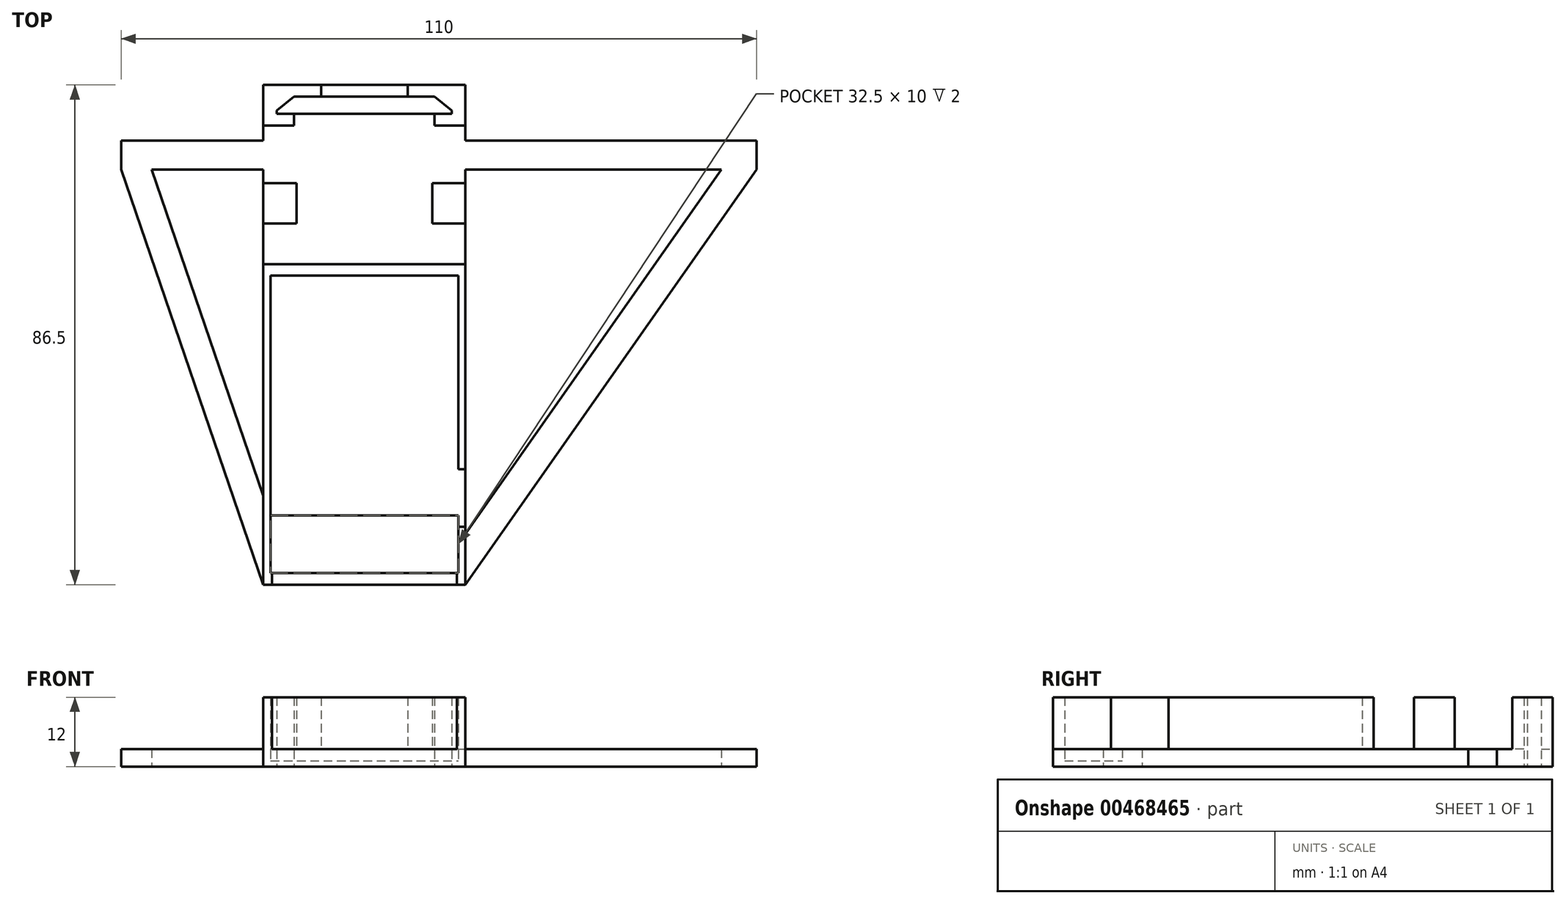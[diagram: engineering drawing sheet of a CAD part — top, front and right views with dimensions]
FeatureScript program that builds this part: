
annotation { "Feature Type Name" : "Feature", "Feature Type Description" : "" }
export const myFeature = defineFeature(function(context is Context, id is Id, definition is map)
    precondition{}
    {
        {
            var Q0;
            Q0=qCreatedBy(makeId("Top.planeOp"),FACE);
            var sketch = newSketch(context, id + "F0", { "sketchPlane" : qUnion([Q0])});
            skLineSegment(sketch, "E0", {"start": v(0, 43.25) * mm, "end": v(-17.5, 43.25) * mm});
            skLineSegment(sketch, "E1", {"start": v(-17.5, 43.25) * mm, "end": v(-17.5, 0) * mm});
            skLineSegment(sketch, "E2", {"start": v(-17.5, 0) * mm, "end": v(-17.5, -43.25) * mm});
            skLineSegment(sketch, "E3", {"start": v(-17.5, 33.6) * mm, "end": v(-42.1, 33.6) * mm});
            skLineSegment(sketch, "E4", {"start": v(-42.1, 33.6) * mm, "end": v(-42.1, 28.6) * mm});
            skLineSegment(sketch, "E5", {"start": v(-42.1, 28.6) * mm, "end": v(-17.5, 28.6) * mm});
            skLineSegment(sketch, "E6", {"start": v(-17.5, -43.25) * mm, "end": v(0, -43.25) * mm});
            skLineSegment(sketch, "E7", {"start": v(-42.1, 28.6) * mm, "end": v(-17.5, -43.25) * mm});
            skLineSegment(sketch, "E8", {"start": v(-17.5, -43.25) * mm, "end": v(-17.5, -27.82) * mm});
            skLineSegment(sketch, "E9", {"start": v(-17.5, -27.82) * mm, "end": v(-36.82, 28.6) * mm});
            skLineSegment(sketch, "E10", {"start": v(-37.1, 33.6) * mm, "end": v(-37.1, 28.6) * mm});
            skLineSegment(sketch, "E11.MirrorCS", {"start": v(17.5, -34.54) * mm, "end": v(61.78, 28.6) * mm});
            skLineSegment(sketch, "E12.MirrorCS", {"start": v(17.5, -43.25) * mm, "end": v(17.5, -34.54) * mm});
            skLineSegment(sketch, "E13.MirrorCS", {"start": v(0, 43.25) * mm, "end": v(17.5, 43.25) * mm});
            skLineSegment(sketch, "E14.MirrorCS", {"start": v(67.9, 28.6) * mm, "end": v(17.5, -43.25) * mm});
            skLineSegment(sketch, "E15.MirrorCS", {"start": v(17.5, 43.25) * mm, "end": v(17.5, 0) * mm});
            skLineSegment(sketch, "E16.MirrorCS", {"start": v(17.5, 0) * mm, "end": v(17.5, -43.25) * mm});
            skLineSegment(sketch, "E17.MirrorCS", {"start": v(62.9, 33.6) * mm, "end": v(62.9, 28.6) * mm});
            skLineSegment(sketch, "E18.MirrorCS", {"start": v(17.5, -43.25) * mm, "end": v(0, -43.25) * mm});
            skLineSegment(sketch, "E19.MirrorCS", {"start": v(67.9, 28.6) * mm, "end": v(17.5, 28.6) * mm});
            skLineSegment(sketch, "E20.MirrorCS", {"start": v(67.9, 33.6) * mm, "end": v(67.9, 28.6) * mm});
            skLineSegment(sketch, "E21.MirrorCS", {"start": v(17.5, 33.6) * mm, "end": v(67.9, 33.6) * mm});
            skLineSegment(sketch, "E22", {"start": v(0, 41.25) * mm, "end": v(12.15, 41.25) * mm});
            skLineSegment(sketch, "E23", {"start": v(12.15, 41.25) * mm, "end": v(15.15, 38.85) * mm});
            skLineSegment(sketch, "E24", {"start": v(15.15, 38.85) * mm, "end": v(15.15, 38.25) * mm});
            skLineSegment(sketch, "E25", {"start": v(15.15, 38.25) * mm, "end": v(0, 38.25) * mm});
            skLineSegment(sketch, "E26.MirrorCS", {"start": v(-15.15, 38.85) * mm, "end": v(-15.15, 38.25) * mm});
            skLineSegment(sketch, "E27.MirrorCS", {"start": v(0, 41.25) * mm, "end": v(-12.15, 41.25) * mm});
            skLineSegment(sketch, "E28.MirrorCS", {"start": v(-15.15, 38.25) * mm, "end": v(0, 38.25) * mm});
            skLineSegment(sketch, "E29.MirrorCS", {"start": v(-12.15, 41.25) * mm, "end": v(-15.15, 38.85) * mm});
            skLineSegment(sketch, "E30", {"start": v(-7.5, 43.25) * mm, "end": v(-7.5, 41.25) * mm});
            skLineSegment(sketch, "E31", {"start": v(-12.15, 36.25) * mm, "end": v(-17.5, 36.25) * mm});
            skLineSegment(sketch, "E32.MirrorCS", {"start": v(12.15, 36.25) * mm, "end": v(17.5, 36.25) * mm});
            skLineSegment(sketch, "E33.MirrorCS", {"start": v(7.5, 43.25) * mm, "end": v(7.5, 41.25) * mm});
            skLineSegment(sketch, "E34", {"start": v(0, -41.25) * mm, "end": v(-16.25, -41.25) * mm});
            skLineSegment(sketch, "E35", {"start": v(-16.25, -41.25) * mm, "end": v(-16.25, 10.25) * mm});
            skLineSegment(sketch, "E36", {"start": v(-16.25, 10.25) * mm, "end": v(0, 10.25) * mm});
            skLineSegment(sketch, "E37.MirrorCS", {"start": v(0, -41.25) * mm, "end": v(16.25, -41.25) * mm});
            skLineSegment(sketch, "E38.MirrorCS", {"start": v(16.25, 10.25) * mm, "end": v(0, 10.25) * mm});
            skLineSegment(sketch, "E39.MirrorCS", {"start": v(16.25, -41.25) * mm, "end": v(16.25, 10.25) * mm});
            skLineSegment(sketch, "E40", {"start": v(17.5, -33.25) * mm, "end": v(16.25, -33.25) * mm});
            skLineSegment(sketch, "E41", {"start": v(17.5, -23.25) * mm, "end": v(16.25, -23.25) * mm});
            skLineSegment(sketch, "E42", {"start": v(-16.25, -31.25) * mm, "end": v(16.25, -31.25) * mm});
            skLineSegment(sketch, "E43", {"start": v(-17.5, 12.25) * mm, "end": v(17.5, 12.25) * mm});
            skLineSegment(sketch, "E44", {"start": v(-16, -41.25) * mm, "end": v(-16, -43.25) * mm});
            skLineSegment(sketch, "E45.MirrorCS", {"start": v(16, -41.25) * mm, "end": v(16, -43.25) * mm});
            skLineSegment(sketch, "E46", {"start": v(-12.15, 36.25) * mm, "end": v(-12.15, 38.25) * mm});
            skLineSegment(sketch, "E47", {"start": v(12.15, 36.25) * mm, "end": v(12.15, 38.25) * mm});
            skLineSegment(sketch, "E48", {"start": v(-17.5, 26.25) * mm, "end": v(-11.75, 26.25) * mm});
            skLineSegment(sketch, "E49.MirrorCS", {"start": v(17.5, 26.25) * mm, "end": v(11.75, 26.25) * mm});
            skLineSegment(sketch, "E50", {"start": v(-11.75, 19.25) * mm, "end": v(-17.5, 19.25) * mm});
            skPoint(sketch, "E50.endSnap0", {"position": v(-17.5, 21.63) * mm});
            skLineSegment(sketch, "E51", {"start": v(11.75, 19.25) * mm, "end": v(17.5, 19.25) * mm});
            skLineSegment(sketch, "E52", {"start": v(-11.75, 26.25) * mm, "end": v(-11.75, 19.25) * mm});
            skLineSegment(sketch, "E53", {"start": v(11.75, 26.25) * mm, "end": v(11.75, 19.25) * mm});
            skSolve(sketch);
        }
        {
            var Q0;
            {var subQ7=sQuery(id+"F0.wireOp",EDGE,"E26.MirrorCS");Q0=makeQuery(id+"F0.imprint","IMPRINT",FACE,{"disambiguationData":[TD([[makeQuery(id+"F0.imprint","IMPRINT",EDGE,{"derivedFrom":subQ7}),-1.0]])]});}
            var Q1;
            {var subQ3=sQuery(id+"F0.wireOp",EDGE,"E30");Q1=makeQuery(id+"F0.imprint","IMPRINT",FACE,{"disambiguationData":[TD([[makeQuery(id+"F0.imprint","IMPRINT",EDGE,{"derivedFrom":subQ3}),1.0]])]});}
            var Q2;
            {var subQ0=sQuery(id+"F0.wireOp",EDGE,"E23");Q2=makeQuery(id+"F0.imprint","IMPRINT",FACE,{"disambiguationData":[TD([[makeQuery(id+"F0.imprint","IMPRINT",EDGE,{"derivedFrom":subQ0}),1.0]])]});}
            var Q3;
            {var subQ1=sQuery(id+"F0.wireOp",EDGE,"fqxOtDsU-wHGC-yRUm-2BCM-Caq6WvGUI0ms");Q3=makeQuery(id+"F0.imprint","IMPRINT",FACE,{"disambiguationData":[TD([[makeQuery(id+"F0.imprint","IMPRINT",EDGE,{"derivedFrom":subQ1}),1.0]])]});}
            var Q4;
            {var subQ9=sQuery(id+"F0.wireOp",EDGE,"E2");Q4=makeQuery(id+"F0.imprint","IMPRINT",FACE,{"disambiguationData":[TD([[makeQuery(id+"F0.imprint","IMPRINT",EDGE,{"derivedFrom":subQ9}),1.0]])]});}
            var Q5;
            {var subQ3=sQuery(id+"F0.wireOp",EDGE,"E40");Q5=makeQuery(id+"F0.imprint","IMPRINT",FACE,{"disambiguationData":[TD([[makeQuery(id+"F0.imprint","IMPRINT",EDGE,{"derivedFrom":subQ3}),-1.0]])]});}
            var Q6;
            {var subQ3=sQuery(id+"F0.wireOp",EDGE,"E11.MirrorCS");Q6=makeQuery(id+"F0.imprint","IMPRINT",FACE,{"disambiguationData":[TD([[makeQuery(id+"F0.imprint","IMPRINT",EDGE,{"derivedFrom":subQ3}),-1.0]])]});}
            var Q7;
            {var subQ2=sQuery(id+"F0.wireOp",EDGE,"E10");Q7=makeQuery(id+"F0.imprint","IMPRINT",FACE,{"disambiguationData":[TD([[makeQuery(id+"F0.imprint","IMPRINT",EDGE,{"derivedFrom":subQ2}),1.0]])]});}
            var Q8;
            {var subQ0=sQuery(id+"F0.wireOp",EDGE,"E4");Q8=makeQuery(id+"F0.imprint","IMPRINT",FACE,{"disambiguationData":[TD([[makeQuery(id+"F0.imprint","IMPRINT",EDGE,{"derivedFrom":subQ0}),1.0]])]});}
            var Q9;
            {var subQ0=sQuery(id+"F0.wireOp",EDGE,"E17.MirrorCS");Q9=makeQuery(id+"F0.imprint","IMPRINT",FACE,{"disambiguationData":[TD([[makeQuery(id+"F0.imprint","IMPRINT",EDGE,{"derivedFrom":subQ0}),1.0]])]});}
            var Q10;
            {var subQ6=sQuery(id+"F0.wireOp",EDGE,"E17.MirrorCS");Q10=makeQuery(id+"F0.imprint","IMPRINT",FACE,{"disambiguationData":[TD([[makeQuery(id+"F0.imprint","IMPRINT",EDGE,{"derivedFrom":subQ6}),-1.0]])]});}
            var Q11;
            {var subQ4=sQuery(id+"F0.wireOp",EDGE,"E36");Q11=makeQuery(id+"F0.imprint","IMPRINT",FACE,{"disambiguationData":[TD([[makeQuery(id+"F0.imprint","IMPRINT",EDGE,{"derivedFrom":subQ4}),-1.0]])]});}
            var Q12;
            {var subQ0=sQuery(id+"F0.wireOp",EDGE,"E7");Q12=makeQuery(id+"F0.imprint","IMPRINT",FACE,{"disambiguationData":[TD([[makeQuery(id+"F0.imprint","IMPRINT",EDGE,{"derivedFrom":subQ0}),1.0]])]});}
            var Q13;
            {var subQ4=sQuery(id+"F0.wireOp",EDGE,"E44");Q13=makeQuery(id+"F0.imprint","IMPRINT",FACE,{"disambiguationData":[TD([[makeQuery(id+"F0.imprint","IMPRINT",EDGE,{"derivedFrom":subQ4}),1.0]])]});}
            var Q14;
            {var subQ3=sQuery(id+"F0.wireOp",EDGE,"E40");Q14=makeQuery(id+"F0.imprint","IMPRINT",FACE,{"disambiguationData":[TD([[makeQuery(id+"F0.imprint","IMPRINT",EDGE,{"derivedFrom":subQ3}),1.0]])]});}
            var Q15;
            {var subQ1=sQuery(id+"F0.wireOp",EDGE,"E31");Q15=makeQuery(id+"F0.imprint","IMPRINT",FACE,{"disambiguationData":[TD([[makeQuery(id+"F0.imprint","IMPRINT",EDGE,{"derivedFrom":subQ1}),1.0]])]});}
            var Q16;
            {var subQ0=sQuery(id+"F0.wireOp",EDGE,"E48");Q16=makeQuery(id+"F0.imprint","IMPRINT",FACE,{"disambiguationData":[TD([[makeQuery(id+"F0.imprint","IMPRINT",EDGE,{"derivedFrom":subQ0}),-1.0]])]});}
            var Q17;
            {var subQ0=sQuery(id+"F0.wireOp",EDGE,"E49.MirrorCS");Q17=makeQuery(id+"F0.imprint","IMPRINT",FACE,{"disambiguationData":[TD([[makeQuery(id+"F0.imprint","IMPRINT",EDGE,{"derivedFrom":subQ0}),1.0]])]});}
            extrude(context, id + "F1", {"entities" : qUnion([Q0, Q1, Q2, Q3, Q4, Q5, Q6, Q7, Q8, Q9, Q10, Q11, Q12, Q13, Q14, Q15, Q16, Q17]), "depth" : 3 * mm, "offsetDistance" : 25 * mm});
        }
        {
            var Q0;
            {var subQ3=sQuery(id+"F0.wireOp",EDGE,"E42");Q0=makeQuery(id+"F0.imprint","IMPRINT",FACE,{"disambiguationData":[TD([[makeQuery(id+"F0.imprint","IMPRINT",EDGE,{"derivedFrom":subQ3}),-1.0]])]});}
            extrude(context, id + "F2", {"entities" : qUnion([Q0]), "operationType" : NewBodyOperationType.ADD, "depth" : 1 * mm, "offsetDistance" : 25 * mm});
        }
        {
            var Q0;
            {var subQ7=sQuery(id+"F0.wireOp",EDGE,"E26.MirrorCS");Q0=makeQuery(id+"F0.imprint","IMPRINT",FACE,{"disambiguationData":[TD([[makeQuery(id+"F0.imprint","IMPRINT",EDGE,{"derivedFrom":subQ7}),-1.0]])]});}
            var Q1;
            {var subQ0=sQuery(id+"F0.wireOp",EDGE,"E23");Q1=makeQuery(id+"F0.imprint","IMPRINT",FACE,{"disambiguationData":[TD([[makeQuery(id+"F0.imprint","IMPRINT",EDGE,{"derivedFrom":subQ0}),1.0]])]});}
            var Q2;
            {var subQ9=sQuery(id+"F0.wireOp",EDGE,"E2");Q2=makeQuery(id+"F0.imprint","IMPRINT",FACE,{"disambiguationData":[TD([[makeQuery(id+"F0.imprint","IMPRINT",EDGE,{"derivedFrom":subQ9}),1.0]])]});}
            var Q3;
            {var subQ3=sQuery(id+"F0.wireOp",EDGE,"E40");Q3=makeQuery(id+"F0.imprint","IMPRINT",FACE,{"disambiguationData":[TD([[makeQuery(id+"F0.imprint","IMPRINT",EDGE,{"derivedFrom":subQ3}),1.0]])]});}
            var Q4;
            {var subQ0=sQuery(id+"F0.wireOp",EDGE,"E48");Q4=makeQuery(id+"F0.imprint","IMPRINT",FACE,{"disambiguationData":[TD([[makeQuery(id+"F0.imprint","IMPRINT",EDGE,{"derivedFrom":subQ0}),-1.0]])]});}
            var Q5;
            {var subQ0=sQuery(id+"F0.wireOp",EDGE,"E49.MirrorCS");Q5=makeQuery(id+"F0.imprint","IMPRINT",FACE,{"disambiguationData":[TD([[makeQuery(id+"F0.imprint","IMPRINT",EDGE,{"derivedFrom":subQ0}),1.0]])]});}
            extrude(context, id + "F3", {"entities" : qUnion([Q0, Q1, Q2, Q3, Q4, Q5]), "operationType" : NewBodyOperationType.ADD, "depth" : 12 * mm, "offsetDistance" : 25 * mm});
        }
    });
